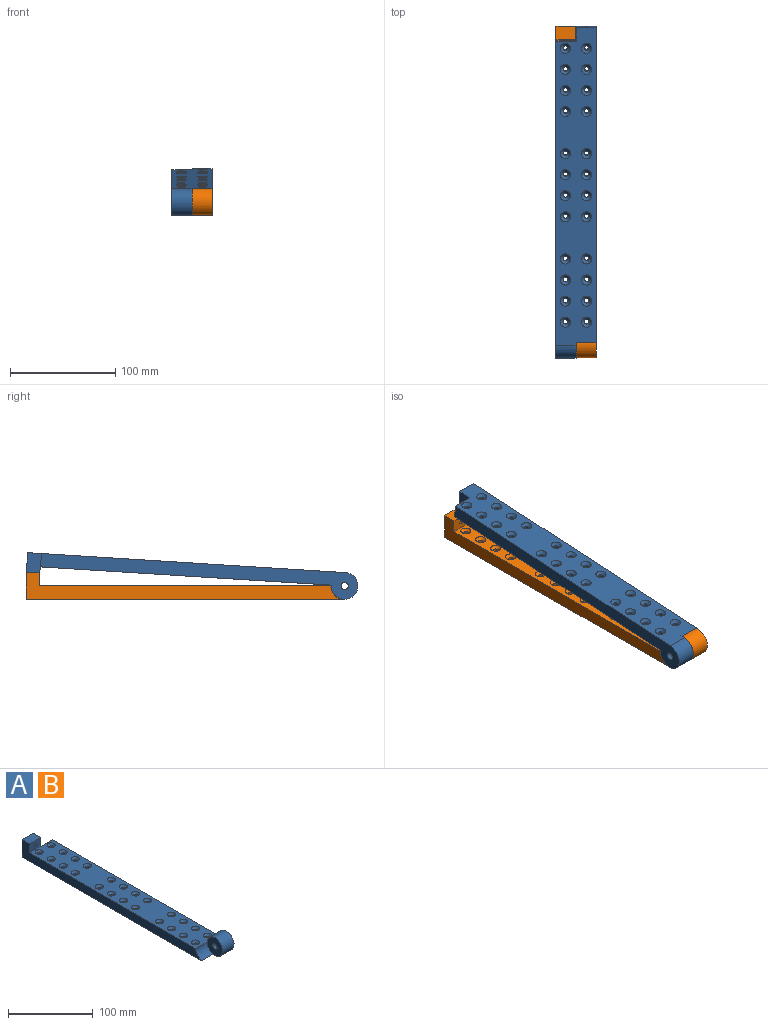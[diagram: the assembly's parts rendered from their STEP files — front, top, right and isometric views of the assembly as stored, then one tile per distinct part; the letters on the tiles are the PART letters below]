
ASSEMBLY  parts=2 mates=1
PART A: 89 faces, bbox 38.1x315.5x25.4 mm
  f0: plane 302.36x25.4mm, normal (1,0,0), area 4021.8mm2, adj f1,f58,f60,f80,f84
  f1: plane 277.37x38.1mm, normal (0,0,1), area 8796.1mm2, adj f0,f2,f3,f4,f5,f6,f7,f8
  f2: cone r=2.29mm half-angle=45deg, axis (0,0,1), area 80.3mm2, adj f1,f21
  f3: cone r=2.29mm half-angle=45deg, axis (0,0,1), area 80.3mm2, adj f1,f25
  f4: cone r=2.29mm half-angle=45deg, axis (0,0,1), area 80.3mm2, adj f1,f20
  f5: cone r=2.29mm half-angle=45deg, axis (0,0,1), area 80.3mm2, adj f1,f24
  f6: cone r=2.29mm half-angle=45deg, axis (0,0,1), area 80.3mm2, adj f1,f19
  f7: cone r=2.29mm half-angle=45deg, axis (0,0,1), area 80.3mm2, adj f1,f22
  f8: cone r=2.29mm half-angle=45deg, axis (0,0,1), area 80.3mm2, adj f1,f23
  f9: cone r=2.29mm half-angle=45deg, axis (0,0,1), area 80.3mm2, adj f1,f18
  f10: cone r=2.29mm half-angle=45deg, axis (0,0,-1), area 80.3mm2, adj f25,f60
  f11: cone r=2.29mm half-angle=45deg, axis (0,0,-1), area 80.3mm2, adj f21,f60
  f12: cone r=2.29mm half-angle=45deg, axis (0,0,-1), area 80.3mm2, adj f20,f60
  f13: cone r=2.29mm half-angle=45deg, axis (0,0,-1), area 80.3mm2, adj f24,f60
  f14: cone r=2.29mm half-angle=45deg, axis (0,0,-1), area 80.3mm2, adj f23,f60
  f15: cone r=2.29mm half-angle=45deg, axis (0,0,-1), area 80.3mm2, adj f19,f60
  f16: cone r=2.29mm half-angle=45deg, axis (0,0,-1), area 80.3mm2, adj f18,f60
  f17: cone r=2.29mm half-angle=45deg, axis (0,0,-1), area 80.3mm2, adj f22,f60
  f18: cylinder r=2.29mm len=7.62mm, axis (0,0,1), area 109.4mm2, adj f9,f16
  f19: cylinder r=2.29mm len=7.62mm, axis (0,0,1), area 109.4mm2, adj f6,f15
  f20: cylinder r=2.29mm len=7.62mm, axis (0,0,1), area 109.4mm2, adj f4,f12
  f21: cylinder r=2.29mm len=7.62mm, axis (0,0,1), area 109.4mm2, adj f2,f11
  f22: cylinder r=2.29mm len=7.62mm, axis (0,0,1), area 109.4mm2, adj f7,f17
  f23: cylinder r=2.29mm len=7.62mm, axis (0,0,1), area 109.4mm2, adj f8,f14
  f24: cylinder r=2.29mm len=7.62mm, axis (0,0,1), area 109.4mm2, adj f5,f13
  f25: cylinder r=2.29mm len=7.62mm, axis (0,0,1), area 109.4mm2, adj f3,f10
  f26: cone r=2.29mm half-angle=45deg, axis (0,0,1), area 80.3mm2, adj f1,f45
  f27: cone r=2.29mm half-angle=45deg, axis (0,0,1), area 80.3mm2, adj f1,f49
  f28: cone r=2.29mm half-angle=45deg, axis (0,0,1), area 80.3mm2, adj f1,f44
  f29: cone r=2.29mm half-angle=45deg, axis (0,0,1), area 80.3mm2, adj f1,f48
  f30: cone r=2.29mm half-angle=45deg, axis (0,0,1), area 80.3mm2, adj f1,f43
  f31: cone r=2.29mm half-angle=45deg, axis (0,0,1), area 80.3mm2, adj f1,f46
  f32: cone r=2.29mm half-angle=45deg, axis (0,0,1), area 80.3mm2, adj f1,f47
  f33: cone r=2.29mm half-angle=45deg, axis (0,0,1), area 80.3mm2, adj f1,f42
  f34: cone r=2.29mm half-angle=45deg, axis (0,0,-1), area 80.3mm2, adj f49,f60
  f35: cone r=2.29mm half-angle=45deg, axis (0,0,-1), area 80.3mm2, adj f45,f60
  f36: cone r=2.29mm half-angle=45deg, axis (0,0,-1), area 80.3mm2, adj f44,f60
  f37: cone r=2.29mm half-angle=45deg, axis (0,0,-1), area 80.3mm2, adj f48,f60
  f38: cone r=2.29mm half-angle=45deg, axis (0,0,-1), area 80.3mm2, adj f47,f60
  f39: cone r=2.29mm half-angle=45deg, axis (0,0,-1), area 80.3mm2, adj f43,f60
  f40: cone r=2.29mm half-angle=45deg, axis (0,0,-1), area 80.3mm2, adj f42,f60
  f41: cone r=2.29mm half-angle=45deg, axis (0,0,-1), area 80.3mm2, adj f46,f60
  f42: cylinder r=2.29mm len=7.62mm, axis (0,0,1), area 109.4mm2, adj f33,f40
  f43: cylinder r=2.29mm len=7.62mm, axis (0,0,1), area 109.4mm2, adj f30,f39
  f44: cylinder r=2.29mm len=7.62mm, axis (0,0,1), area 109.4mm2, adj f28,f36
  f45: cylinder r=2.29mm len=7.62mm, axis (0,0,1), area 109.4mm2, adj f26,f35
  f46: cylinder r=2.29mm len=7.62mm, axis (0,0,1), area 109.4mm2, adj f31,f41
  f47: cylinder r=2.29mm len=7.62mm, axis (0,0,1), area 109.4mm2, adj f32,f38
  f48: cylinder r=2.29mm len=7.62mm, axis (0,0,1), area 109.4mm2, adj f29,f37
  f49: cylinder r=2.29mm len=7.62mm, axis (0,0,1), area 109.4mm2, adj f27,f34
  f50: cylinder r=2.29mm len=7.62mm, axis (0,0,1), area 109.4mm2, adj f65,f72
  f51: cylinder r=2.29mm len=7.62mm, axis (0,0,1), area 109.4mm2, adj f66,f75
  f52: cylinder r=2.29mm len=7.62mm, axis (0,0,1), area 109.4mm2, adj f69,f77
  f53: cylinder r=2.29mm len=7.62mm, axis (0,0,1), area 109.4mm2, adj f70,f79
  f54: cylinder r=2.29mm len=7.62mm, axis (0,0,1), area 109.4mm2, adj f64,f74
  f55: cylinder r=2.29mm len=7.62mm, axis (0,0,1), area 109.4mm2, adj f67,f73
  f56: cylinder r=2.29mm len=7.62mm, axis (0,0,1), area 109.4mm2, adj f68,f76
  f57: plane 299.53x25.4mm, normal (-1,0,0), area 3872.4mm2, adj f1,f59,f60,f61,f81,f83
  f58: cylinder r=12.7mm len=25.4mm, axis (-1,0,0), area 1140.1mm2, adj f0,f1,f60,f62
  f59: plane 25.4x18.85mm, normal (0,1,0), area 461mm2, adj f57,f60,f82,f83,f85,f86,f88
  f60: plane 302.77x38.1mm, normal (0,0,-1), area 9465.4mm2, adj f0,f10,f11,f12,f13,f14,f15,f16
  f61: cylinder r=13.11mm len=19.05mm, axis (-1,0,0), area 329.9mm2, adj f1,f57,f60,f62
  f62: plane 25.81x25.4mm, normal (-1,0,0), area 477.1mm2, adj f1,f58,f60,f61,f80
  f63: cylinder r=2.29mm len=7.62mm, axis (0,0,1), area 109.4mm2, adj f71,f78
  f64: cone r=2.29mm half-angle=45deg, axis (0,0,-1), area 80.3mm2, adj f54,f60
  f65: cone r=2.29mm half-angle=45deg, axis (0,0,-1), area 80.3mm2, adj f50,f60
  f66: cone r=2.29mm half-angle=45deg, axis (0,0,-1), area 80.3mm2, adj f51,f60
  f67: cone r=2.29mm half-angle=45deg, axis (0,0,-1), area 80.3mm2, adj f55,f60
  f68: cone r=2.29mm half-angle=45deg, axis (0,0,-1), area 80.3mm2, adj f56,f60
  f69: cone r=2.29mm half-angle=45deg, axis (0,0,-1), area 80.3mm2, adj f52,f60
  f70: cone r=2.29mm half-angle=45deg, axis (0,0,-1), area 80.3mm2, adj f53,f60
  f71: cone r=2.29mm half-angle=45deg, axis (0,0,-1), area 80.3mm2, adj f60,f63
  f72: cone r=2.29mm half-angle=45deg, axis (0,0,1), area 80.3mm2, adj f1,f50
  f73: cone r=2.29mm half-angle=45deg, axis (0,0,1), area 80.3mm2, adj f1,f55
  f74: cone r=2.29mm half-angle=45deg, axis (0,0,1), area 80.3mm2, adj f1,f54
  f75: cone r=2.29mm half-angle=45deg, axis (0,0,1), area 80.3mm2, adj f1,f51
  f76: cone r=2.29mm half-angle=45deg, axis (0,0,1), area 80.3mm2, adj f1,f56
  f77: cone r=2.29mm half-angle=45deg, axis (0,0,1), area 80.3mm2, adj f1,f52
  f78: cone r=2.29mm half-angle=45deg, axis (0,0,1), area 80.3mm2, adj f1,f63
  f79: cone r=2.29mm half-angle=45deg, axis (0,0,1), area 80.3mm2, adj f1,f53
  f80: cylinder r=3.43mm len=19.05mm, axis (-1,0,0), area 410.4mm2, adj f0,f62
  f81: plane 18.85x12.7mm, normal (0,-1,0), area 230.2mm2, adj f1,f57,f82,f83,f85,f88
  f82: plane 22.86x13.11mm, normal (1,0,0), area 295.5mm2, adj f1,f59,f60,f81,f84,f88
  f83: plane 18.4x12.7mm, normal (0,0,1), area 233.7mm2, adj f57,f59,f81,f88
  f84: plane 19.25x12.7mm, normal (0,1,0), area 244.5mm2, adj f0,f1,f60,f82
  f85: cylinder r=1.65mm len=12.7mm, axis (0,1,0), area 131.7mm2, adj f59,f81
  f86: cylinder r=1.65mm len=15.24mm, axis (0,1,0), area 158.1mm2, adj f59,f87
  f87: plane 3.3x3.3mm, normal (0,1,0), area 8.6mm2, adj f86
  f88: plane 12.7x2.54mm, normal (0.98,0,0.17), area 32.8mm2, adj f59,f81,f82,f83
PART B: same geometry as A
PLACE A rot(axis=(0,1,0.03),180deg) t=(80.26,-6.11,194.73)mm
PLACE B at identity fixed
MATE revolute A.f58 <-> B.f58  axis (1,0,0) through (40.13,-293.12,88.27)mm
